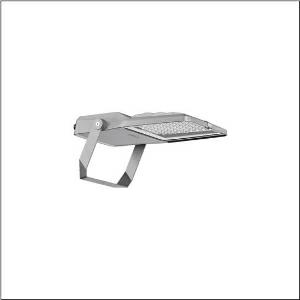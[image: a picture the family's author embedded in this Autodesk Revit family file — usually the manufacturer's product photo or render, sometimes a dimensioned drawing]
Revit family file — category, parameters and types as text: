
# Revit family: floodlight_fl_21_iq_mini___pl43_5xa7772b3a1a_8813
name_source: partatom
category: Lighting Fixtures
units: mm (PartAtom-declared; Revit-internal decimal feet)

## family parameters
Cut with Voids When Loaded = No
Host = Face
Light Source = No
Part Type = Normal
Room Calculation Point = No
Round Connector Dimension = Use Diameter
Shared = No

## types (1)
- --- (1 x LED, 5510 lm, 45.5 W, 3000K)
    Apparent Load = 46 VA
    CIE Flux Codes = 27 78 99 100 100
    Color Rendering = 80
    Color Temperature = 3000K
    Default Elevation = 1800 mm
    Description = Floodlight FL 21 iQ mini, floodlight, primary light control with lens, of PMMA, primary optical cover: protective disc, of toughened safety glass, transparent, light distribution: PL43, light emission: direct distribution, installation type: surface-mounted, LED, High Power LED, rated luminous flux: 5.510lm, luminous efficacy: 121lm/W, light colour: 830, colour temperature: 3000K, control gear: iQ Street-Remote/DALI, control: Street-Remote, Auto-Match, Temp-Guard, Night-Set, Smart-Wire, Desk-Remote (wireless, voltage-free reading and setting of iQ features in the workshop via application-optimized NFC function/RFID function), optimised constant luminous flux control (CLO 2.0), with terminal, 6-pole, mains connection: 220..240V, AC, 50/60Hz, start of lifetime: 46W, end of service life: 48W, reduction: 21W, luminaire housing, of diecast aluminium, powder-coated, Siteco® metallic grey (DB 702S), corrosivity category C5 mid according to DIN EN ISO 12944, suitable for swimming pools, chlorine-resistant, sealing non-destructively replaceable, mounting bracket, of steel, galvanised, powder-coated, Siteco® metallic grey (DB 702S), protection rating (complete): IP66, insulation class (complete): insulation class II (safety insulation), certification: CE, ENEC, VDE, protection symbol: D, impact resistance: IK08, permissible operating ambient temperature: -40..+40°C, permissible operating ambient temperature for outdoor applications: -40..+50°C, standard: DIN EN 12944, LABS conformity tested according to VDMA 24364:2018-05, packaging unit: 1 piece

Light Distribution: PL43
    Height = 70 mm
    Lamp = 1 x LED
    Lamp Light Flux = 5510 lm
    Lamp Power = 45.5 W
    Lamp count = 1
    Length = 485 mm
    Luminous efficacy = 121 lm/W
    Manufacturer = Siteco
    ModVariant = No
    Model = 5XA7772B3A1A
    Number of Poles = 1
    OnlyDefault = Yes
    Power Factor = 1
    Product Name = Floodlight FL 21 iQ mini | PL43
    Product group = floodlight | pylon annexe
    ProductGroupID = 6200
    Protection Class = Protection class II
    Protection Degree = IP 66
    RLX_Detail_Level = 1
    RLX_Emergency_Light_Flux = 0 lm
    RLX_Emergency_Type = 0
    RLX_Emergency_Type_DB = No
    RlxData = <blob elided: 96181 chars, md5=5a69554f>
    Socket = socket
    Standby Power = 0 W
    System Light Flux = 5510 lm
    System Power = 46 W
    Type Comments = factory setting: luminous flux: 100 % | dim-lin: 254 | 463 mA
    Type Image = l_1006845.jpg
    URL = http://relux.com
    VarID = @adj_162754
    Voltage = 0 V
    Weight = 0.00 kg
    Width = 337 mm

## geometry (parser evidence)
native form markers: Blend x4, Sweep x11
no freeform markers — native parametric forms only
